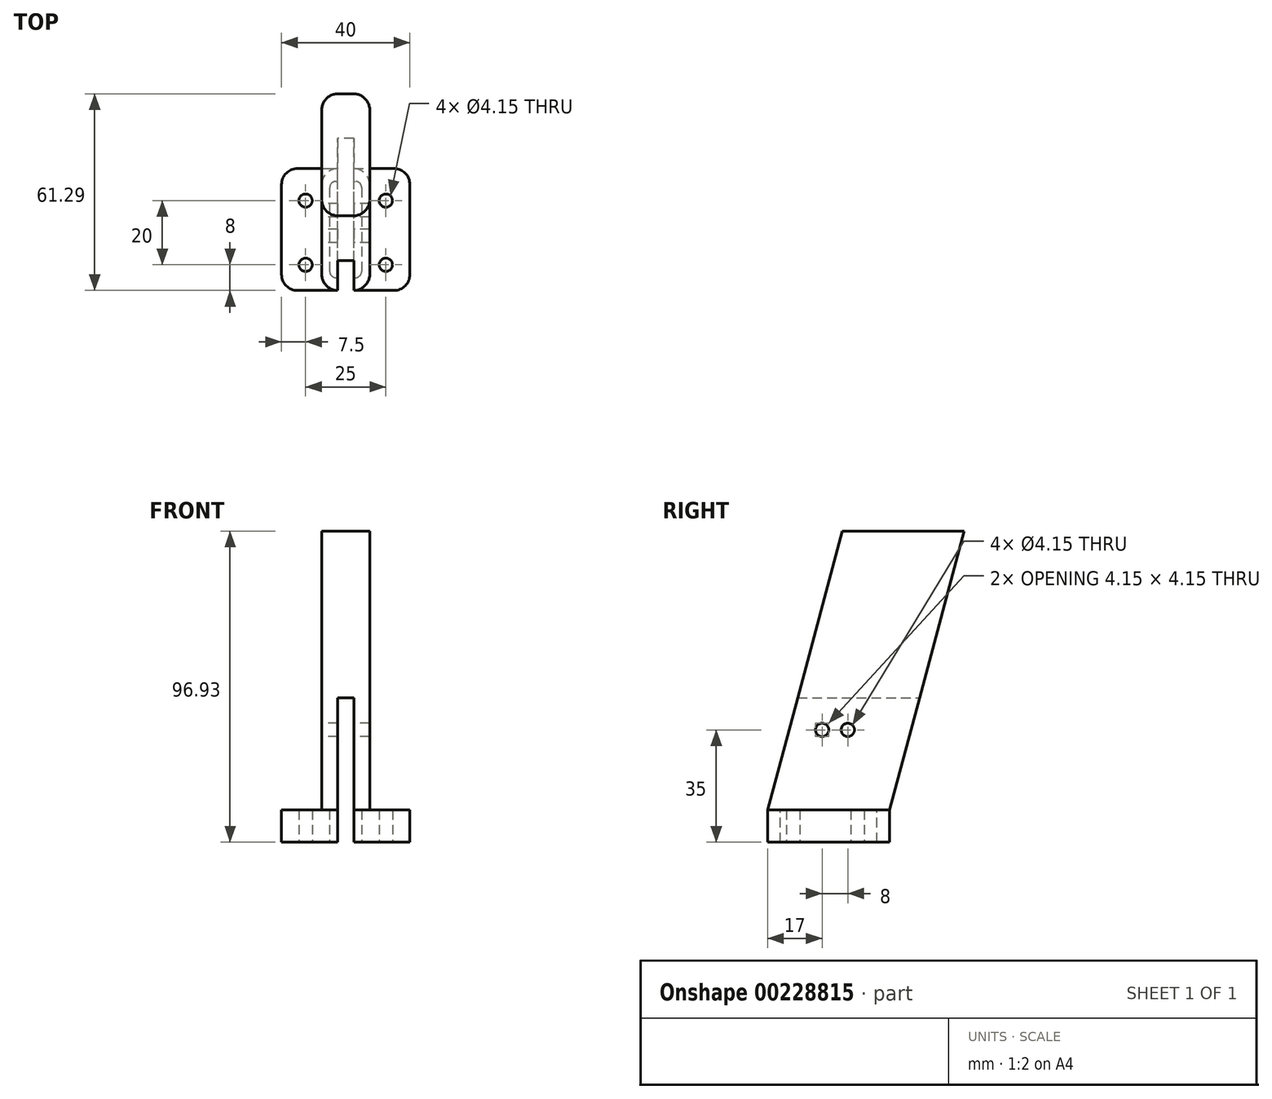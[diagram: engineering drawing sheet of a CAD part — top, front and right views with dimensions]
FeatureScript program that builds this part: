
annotation { "Feature Type Name" : "Feature", "Feature Type Description" : "" }
export const myFeature = defineFeature(function(context is Context, id is Id, definition is map)
    precondition{}
    {
        {
            var Q0;
            Q0=qCreatedBy(makeId("Top.planeOp"),FACE);
            var sketch = newSketch(context, id + "F0", { "sketchPlane" : qUnion([Q0])});
            skLineSegment(sketch, "E0.bottom", {"start": v(-20, 19) * mm, "end": v(20, 19) * mm});
            skLineSegment(sketch, "E0.top", {"start": v(-20, -19) * mm, "end": v(20, -19) * mm});
            skLineSegment(sketch, "E0.left", {"start": v(-20, 19) * mm, "end": v(-20, -19) * mm});
            skLineSegment(sketch, "E0.right", {"start": v(20, 19) * mm, "end": v(20, -19) * mm});
            skCircle(sketch, "E1", {"center": v(-12.5, -11) * mm, "radius": 2.07 * mm});
            skCircle(sketch, "E2", {"center": v(-12.5, 9) * mm, "radius": 2.07 * mm});
            skCircle(sketch, "E3.MirrorC", {"center": v(12.5, 9) * mm, "radius": 2.07 * mm});
            skCircle(sketch, "E4.MirrorC", {"center": v(12.5, -11) * mm, "radius": 2.07 * mm});
            skLineSegment(sketch, "E5.bottom", {"start": v(-5, 15) * mm, "end": v(5, 15) * mm});
            skLineSegment(sketch, "E5.top", {"start": v(-5, -15) * mm, "end": v(5, -15) * mm});
            skLineSegment(sketch, "E5.left", {"start": v(-5, 15) * mm, "end": v(-5, -15) * mm});
            skLineSegment(sketch, "E5.right", {"start": v(5, 15) * mm, "end": v(5, -15) * mm});
            skSolve(sketch);
        }
        {
            var Q0;
            Q0 = qSketchRegion(id + "F0", true);
            extrude(context, id + "F1", {"entities" : qUnion([Q0]), "depth" : 10 * mm});
        }
        {
            var Q0;
            Q0=makeQuery(id+"F1.opExtrude","SWEPT_EDGE",EDGE,{"disambiguationData":[OSD([sQuery(id+"F0.wireOp",EDGE,"E0.bottom"),sQuery(id+"F0.wireOp",EDGE,"E0.left")])]});
            var Q1;
            Q1=makeQuery(id+"F1.opExtrude","SWEPT_EDGE",EDGE,{"disambiguationData":[OSD([sQuery(id+"F0.wireOp",EDGE,"E0.bottom"),sQuery(id+"F0.wireOp",EDGE,"E0.right")])]});
            var Q2;
            Q2=makeQuery(id+"F1.opExtrude","SWEPT_EDGE",EDGE,{"disambiguationData":[OSD([sQuery(id+"F0.wireOp",EDGE,"E0.top"),sQuery(id+"F0.wireOp",EDGE,"E0.right")])]});
            var Q3;
            Q3=makeQuery(id+"F1.opExtrude","SWEPT_EDGE",EDGE,{"disambiguationData":[OSD([sQuery(id+"F0.wireOp",EDGE,"E0.top"),sQuery(id+"F0.wireOp",EDGE,"E0.left")])]});
            fillet(context, id + "F2", {"entities" : qUnion([Q0, Q1, Q2, Q3]), "radius" : 5 * mm, "tangentPropagation" : true, "allowEdgeOverflow" : false});
        }
        {
            var Q0;
            Q0=makeQuery(id+"F1.opExtrude","SWEPT_EDGE",EDGE,{"disambiguationData":[OSD([sQuery(id+"F0.wireOp",EDGE,"E5.bottom"),sQuery(id+"F0.wireOp",EDGE,"E5.left")])]});
            var Q1;
            Q1=makeQuery(id+"F1.opExtrude","SWEPT_EDGE",EDGE,{"disambiguationData":[OSD([sQuery(id+"F0.wireOp",EDGE,"E5.bottom"),sQuery(id+"F0.wireOp",EDGE,"E5.right")])]});
            var Q2;
            Q2=makeQuery(id+"F1.opExtrude","SWEPT_EDGE",EDGE,{"disambiguationData":[OSD([sQuery(id+"F0.wireOp",EDGE,"E5.top"),sQuery(id+"F0.wireOp",EDGE,"E5.left")])]});
            var Q3;
            Q3=makeQuery(id+"F1.opExtrude","SWEPT_EDGE",EDGE,{"disambiguationData":[OSD([sQuery(id+"F0.wireOp",EDGE,"E5.top"),sQuery(id+"F0.wireOp",EDGE,"E5.right")])]});
            fillet(context, id + "F3", {"entities" : qUnion([Q0, Q1, Q2, Q3]), "radius" : 2 * mm, "tangentPropagation" : true, "allowEdgeOverflow" : false});
        }
        {
            var Q0;
            Q0=qCreatedBy(makeId("Right.planeOp"),FACE);
            var sketch = newSketch(context, id + "F4", { "sketchPlane" : qUnion([Q0])});
            skLineSegment(sketch, "E6", {"start": v(4.3, 96.93) * mm, "end": v(-19, 10) * mm});
            skLineSegment(sketch, "E7", {"start": v(42.3, 96.93) * mm, "end": v(19, 10) * mm});
            skLineSegment(sketch, "E8", {"start": v(42.3, 96.93) * mm, "end": v(4.3, 96.93) * mm});
            skLineSegment(sketch, "E9", {"start": v(19, 10) * mm, "end": v(-19, 10) * mm});
            skSolve(sketch);
        }
        {
            var Q0;
            Q0=makeQuery(id+"F4.imprint","IMPRINT",FACE,{"disambiguationData":[TD([[makeQuery(id+"F4.imprint","IMPRINT",EDGE,{"derivedFrom":sQuery(id+"F4.wireOp",EDGE,"E6")}),1.0]])]});
            extrude(context, id + "F5", {"entities" : qUnion([Q0]), "operationType" : NewBodyOperationType.ADD, "endBound" : BoundingType.SYMMETRIC, "depth" : 15 * mm});
        }
        {
            var Q0;
            Q0=makeQuery(id+"F5.opExtrude","CAP_EDGE",EDGE,{"disambiguationData":[OSD([sQuery(id+"F4.wireOp",EDGE,"E6")])],"isStart":true});
            var Q1;
            Q1=makeQuery(id+"F5.opExtrude","CAP_EDGE",EDGE,{"disambiguationData":[OSD([sQuery(id+"F4.wireOp",EDGE,"E6")])],"isStart":false});
            var Q2;
            Q2=makeQuery(id+"F5.opExtrude","CAP_EDGE",EDGE,{"disambiguationData":[OSD([sQuery(id+"F4.wireOp",EDGE,"E7")])],"isStart":true});
            var Q3;
            Q3=makeQuery(id+"F5.opExtrude","CAP_EDGE",EDGE,{"disambiguationData":[OSD([sQuery(id+"F4.wireOp",EDGE,"E7")])],"isStart":false});
            fillet(context, id + "F6", {"entities" : qUnion([Q0, Q1, Q2, Q3]), "radius" : 5 * mm, "tangentPropagation" : true, "allowEdgeOverflow" : false});
        }
        {
            var Q0;
            Q0=qCreatedBy(makeId("Right.planeOp"),FACE);
            var sketch = newSketch(context, id + "F7", { "sketchPlane" : qUnion([Q0])});
            skCircle(sketch, "E10", {"center": v(-2, 35) * mm, "radius": 2.07 * mm});
            skCircle(sketch, "E11", {"center": v(6, 35) * mm, "radius": 2.07 * mm});
            skSolve(sketch);
        }
        {
            var Q0;
            Q0=qCreatedBy(makeId("Front.planeOp"),FACE);
            var sketch = newSketch(context, id + "F8", { "sketchPlane" : qUnion([Q0])});
            skLineSegment(sketch, "E12.bottom", {"start": v(2.5, 0) * mm, "end": v(-2.5, 0) * mm});
            skLineSegment(sketch, "E12.top", {"start": v(2.5, 45) * mm, "end": v(-2.5, 45) * mm});
            skLineSegment(sketch, "E12.left", {"start": v(2.5, 0) * mm, "end": v(2.5, 45) * mm});
            skLineSegment(sketch, "E12.right", {"start": v(-2.5, 0) * mm, "end": v(-2.5, 45) * mm});
            skSolve(sketch);
        }
        {
            var Q0;
            Q0=makeQuery(id+"F8.imprint","IMPRINT",FACE,{"disambiguationData":[TD([[makeQuery(id+"F8.imprint","IMPRINT",EDGE,{"derivedFrom":sQuery(id+"F8.wireOp",EDGE,"E12.bottom")}),-1.0]])]});
            extrude(context, id + "F9", {"entities" : qUnion([Q0]), "operationType" : NewBodyOperationType.REMOVE, "endBound" : BoundingType.SYMMETRIC, "depth" : 100 * mm});
        }
        {
            var Q0;
            Q0 = qSketchRegion(id + "F7", true);
            extrude(context, id + "F10", {"entities" : qUnion([Q0]), "operationType" : NewBodyOperationType.REMOVE, "endBound" : BoundingType.SYMMETRIC, "depth" : 50 * mm});
        }
    });
